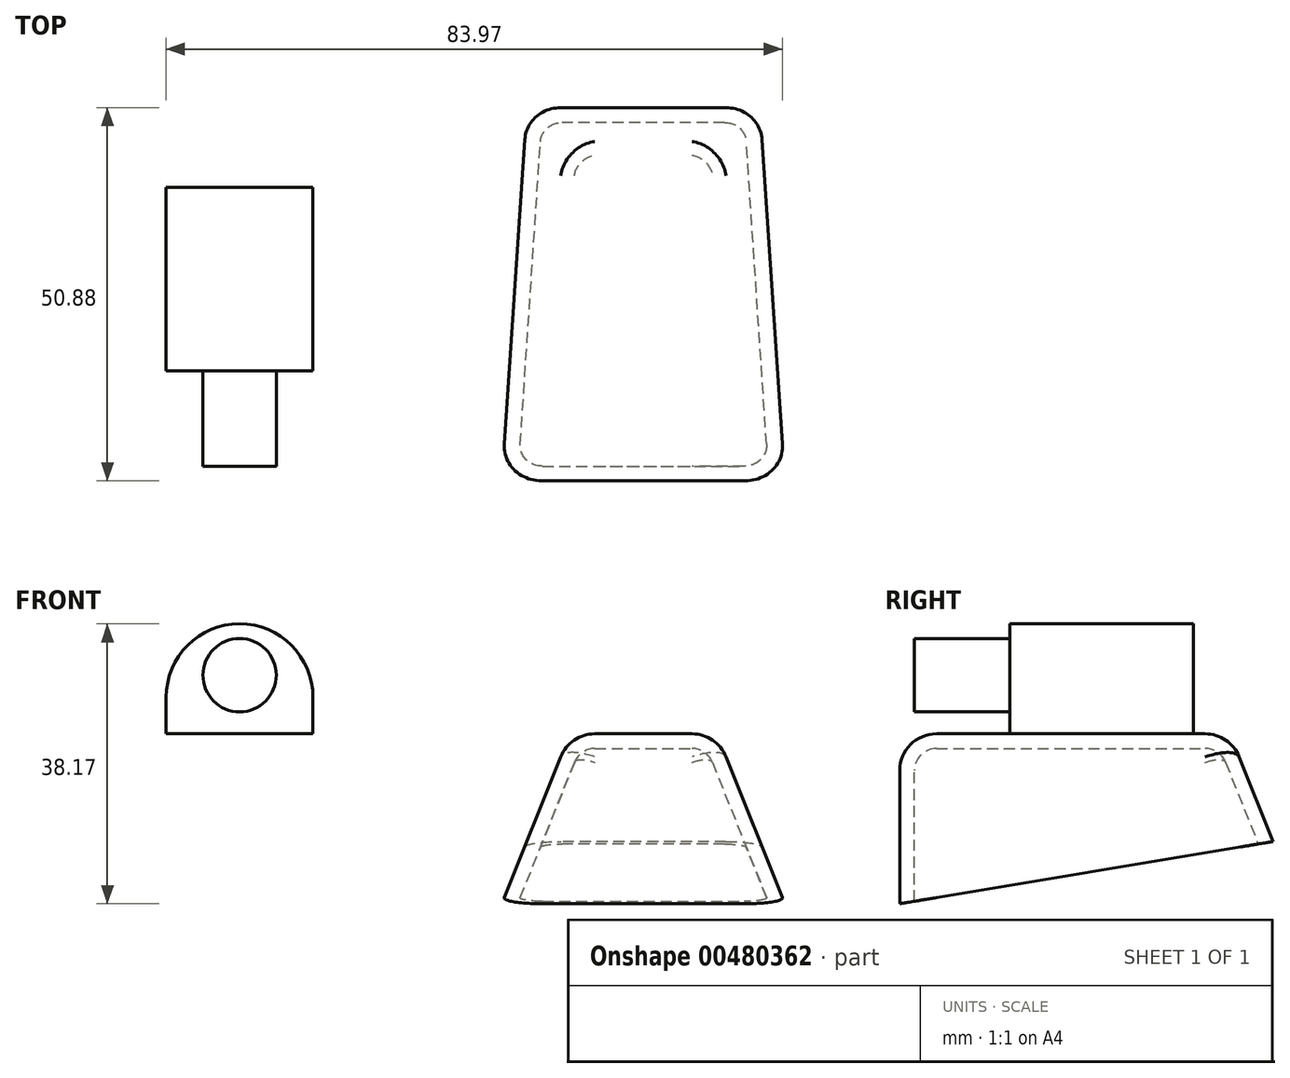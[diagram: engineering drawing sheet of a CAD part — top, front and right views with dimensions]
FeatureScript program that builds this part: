
annotation { "Feature Type Name" : "Feature", "Feature Type Description" : "" }
export const myFeature = defineFeature(function(context is Context, id is Id, definition is map)
    precondition{}
    {
        {
            var Q0;
            Q0=qCreatedBy(makeId("Top.planeOp"),FACE);
            var sketch = newSketch(context, id + "F0", { "sketchPlane" : qUnion([Q0])});
            skLineSegment(sketch, "E0.bottom", {"start": v(10, -17.5) * mm, "end": v(-10, -17.5) * mm, "construction": true});
            skLineSegment(sketch, "E0.top", {"start": v(10, 17.5) * mm, "end": v(-10, 17.5) * mm, "construction": true});
            skLineSegment(sketch, "E0.left", {"start": v(10, -17.5) * mm, "end": v(10, 17.5) * mm, "construction": true});
            skLineSegment(sketch, "E0.right", {"start": v(-10, -17.5) * mm, "end": v(-10, 17.5) * mm, "construction": true});
            skPoint(sketch, "E0.middle", {"position": v(0, 0) * mm});
            skLineSegment(sketch, "E1.0", {"start": v(-20, -27.5) * mm, "end": v(-20, 27.5) * mm});
            skLineSegment(sketch, "E1.1", {"start": v(20, -27.5) * mm, "end": v(-20, -27.5) * mm});
            skLineSegment(sketch, "E1.2", {"start": v(20, -27.5) * mm, "end": v(20, 27.5) * mm});
            skLineSegment(sketch, "E1.3", {"start": v(20, 27.5) * mm, "end": v(-20, 27.5) * mm});
            skLineSegment(sketch, "E2", {"start": v(-20, 27.5) * mm, "end": v(-20, 38.5) * mm});
            skLineSegment(sketch, "E3", {"start": v(-20, 38.5) * mm, "end": v(20, 38.5) * mm});
            skLineSegment(sketch, "E4", {"start": v(20, 38.5) * mm, "end": v(20, 27.5) * mm});
            skLineSegment(sketch, "E5.bottom", {"start": v(-45.03, -12.5) * mm, "end": v(-65.03, -12.5) * mm});
            skLineSegment(sketch, "E5.top", {"start": v(-45.03, 12.5) * mm, "end": v(-65.03, 12.5) * mm});
            skLineSegment(sketch, "E5.left", {"start": v(-45.03, -12.5) * mm, "end": v(-45.03, 12.5) * mm});
            skLineSegment(sketch, "E5.right", {"start": v(-65.03, -12.5) * mm, "end": v(-65.03, 12.5) * mm});
            skPoint(sketch, "E5.middle", {"position": v(-55.03, 0) * mm});
            skSolve(sketch);
        }
        {
            var Q0;
            Q0=makeQuery(id+"F0.imprint","IMPRINT",FACE,{"disambiguationData":[TD([[makeQuery(id+"F0.imprint","IMPRINT",EDGE,{"derivedFrom":sQuery(id+"F0.wireOp",EDGE,"E1.0")}),-1.0]])]});
            extrude(context, id + "F1", {"entities" : qUnion([Q0]), "oppositeDirection" : true, "depth" : 25 * mm});
        }
        {
            var Q0;
            Q0=makeQuery(id+"F1.opExtrude","CAP_EDGE",EDGE,{"disambiguationData":[OSD([sQuery(id+"F0.wireOp",EDGE,"E1.3")])],"isStart":false});
            chamfer(context, id + "F2", {"entities" : qUnion([Q0]), "chamferType" : ChamferType.TWO_OFFSETS, "width1" : 11 * mm, "oppositeDirection" : false, "width2" : 66 * mm, "tangentPropagation" : true});
        }
        {
            var Q0;
            Q0=makeQuery(id+"F1.opExtrude","CAP_EDGE",EDGE,{"disambiguationData":[OSD([sQuery(id+"F0.wireOp",EDGE,"E1.2")])],"isStart":true});
            var Q1;
            Q1=makeQuery(id+"F1.opExtrude","CAP_EDGE",EDGE,{"disambiguationData":[OSD([sQuery(id+"F0.wireOp",EDGE,"E1.0")])],"isStart":true});
            var Q2;
            Q2=makeQuery(id+"F1.opExtrude","CAP_EDGE",EDGE,{"disambiguationData":[OSD([sQuery(id+"F0.wireOp",EDGE,"E1.3")])],"isStart":true});
            chamfer(context, id + "F3", {"entities" : qUnion([Q0, Q1, Q2]), "chamferType" : ChamferType.TWO_OFFSETS, "width1" : 10 * mm, "oppositeDirection" : false, "width2" : 25 * mm, "tangentPropagation" : true});
        }
        {
            var Q0;
            Q0=makeQuery(id+"F1.opExtrude","CAP_FACE",FACE,{"disambiguationData":[OSD([sQuery(id+"F0.wireOp",EDGE,"E1.0"),sQuery(id+"F0.wireOp",EDGE,"E1.1"),sQuery(id+"F0.wireOp",EDGE,"E1.2"),sQuery(id+"F0.wireOp",EDGE,"E1.3")])],"isStart":true});
            var Q1;
            Q1=makeQuery(id+"F3.opChamfer","BLEND_EDGE",EDGE,{"blendedFrom":[makeQuery(id+"F1.opExtrude","CAP_EDGE",EDGE,{"disambiguationData":[OSD([sQuery(id+"F0.wireOp",EDGE,"E1.0")])],"isStart":true}),makeQuery(id+"F1.opExtrude","CAP_EDGE",EDGE,{"disambiguationData":[OSD([sQuery(id+"F0.wireOp",EDGE,"E1.3")])],"isStart":true})],"blendedInto":[]});
            var Q2;
            Q2=makeQuery(id+"F3.opChamfer","BLEND_EDGE",EDGE,{"blendedFrom":[makeQuery(id+"F1.opExtrude","CAP_EDGE",EDGE,{"disambiguationData":[OSD([sQuery(id+"F0.wireOp",EDGE,"E1.2")])],"isStart":true}),makeQuery(id+"F1.opExtrude","CAP_EDGE",EDGE,{"disambiguationData":[OSD([sQuery(id+"F0.wireOp",EDGE,"E1.3")])],"isStart":true})],"blendedInto":[]});
            var Q3;
            Q3=makeQuery(id+"F3.opChamfer","BLEND_EDGE",EDGE,{"blendedFrom":[makeQuery(id+"F1.opExtrude","CAP_EDGE",EDGE,{"disambiguationData":[OSD([sQuery(id+"F0.wireOp",EDGE,"E1.0")])],"isStart":true}),makeQuery(id+"F1.opExtrude","SWEPT_FACE",FACE,{"disambiguationData":[OSD([sQuery(id+"F0.wireOp",EDGE,"E1.1")])]})],"blendedInto":[makeQuery(id+"F1.opExtrude","SWEPT_FACE",FACE,{"disambiguationData":[OSD([sQuery(id+"F0.wireOp",EDGE,"E1.1")])]})]});
            var Q4;
            Q4=makeQuery(id+"F3.opChamfer","BLEND_EDGE",EDGE,{"blendedFrom":[makeQuery(id+"F1.opExtrude","CAP_EDGE",EDGE,{"disambiguationData":[OSD([sQuery(id+"F0.wireOp",EDGE,"E1.2")])],"isStart":true}),makeQuery(id+"F1.opExtrude","SWEPT_FACE",FACE,{"disambiguationData":[OSD([sQuery(id+"F0.wireOp",EDGE,"E1.1")])]})],"blendedInto":[makeQuery(id+"F1.opExtrude","SWEPT_FACE",FACE,{"disambiguationData":[OSD([sQuery(id+"F0.wireOp",EDGE,"E1.1")])]})]});
            fillet(context, id + "F4", {"entities" : qUnion([Q0, Q1, Q2, Q3, Q4]), "radius" : 5 * mm, "tangentPropagation" : true, "allowEdgeOverflow" : false});
        }
        {
            var Q0;
            Q0=makeQuery(id+"F2.opChamfer","BLEND_FACE",FACE,{"disambiguationData":[OSD([sQuery(id+"F0.wireOp",EDGE,"E1.3")])]});
            shell(context, id + "F5", {"entities" : qUnion([Q0]), "thickness" : 2 * mm});
        }
        {
            var Q0;
            Q0=makeQuery(id+"F0.imprint","IMPRINT",FACE,{"disambiguationData":[TD([[makeQuery(id+"F0.imprint","IMPRINT",EDGE,{"derivedFrom":sQuery(id+"F0.wireOp",EDGE,"E5.bottom")}),-1.0]])]});
            extrude(context, id + "F6", {"entities" : qUnion([Q0]), "depth" : 15 * mm, "offsetDistance" : 25 * mm});
        }
        {
            var Q0;
            Q0=makeQuery(id+"F6.opExtrude","CAP_EDGE",EDGE,{"disambiguationData":[OSD([sQuery(id+"F0.wireOp",EDGE,"E5.left")])],"isStart":false});
            var Q1;
            Q1=makeQuery(id+"F6.opExtrude","CAP_EDGE",EDGE,{"disambiguationData":[OSD([sQuery(id+"F0.wireOp",EDGE,"E5.right")])],"isStart":false});
            fillet(context, id + "F7", {"entities" : qUnion([Q0, Q1]), "radius" : 10 * mm, "tangentPropagation" : true, "allowEdgeOverflow" : false});
        }
        {
            var Q0;
            Q0=makeQuery(id+"F6.opExtrude","SWEPT_FACE",FACE,{"disambiguationData":[OSD([sQuery(id+"F0.wireOp",EDGE,"E5.bottom")])]});
            var sketch = newSketch(context, id + "F8", { "sketchPlane" : qUnion([Q0])});
            skCircle(sketch, "E6", {"center": v(-55.03, 8) * mm, "radius": 5 * mm});
            skPoint(sketch, "E7", {"position": v(-55.03, 15) * mm});
            skSolve(sketch);
        }
        {
            var Q0;
            Q0 = qSketchRegion(id + "F8", true);
            extrude(context, id + "F9", {"entities" : qUnion([Q0]), "operationType" : NewBodyOperationType.ADD, "depth" : 13 * mm, "offsetDistance" : 25 * mm});
        }
    });
